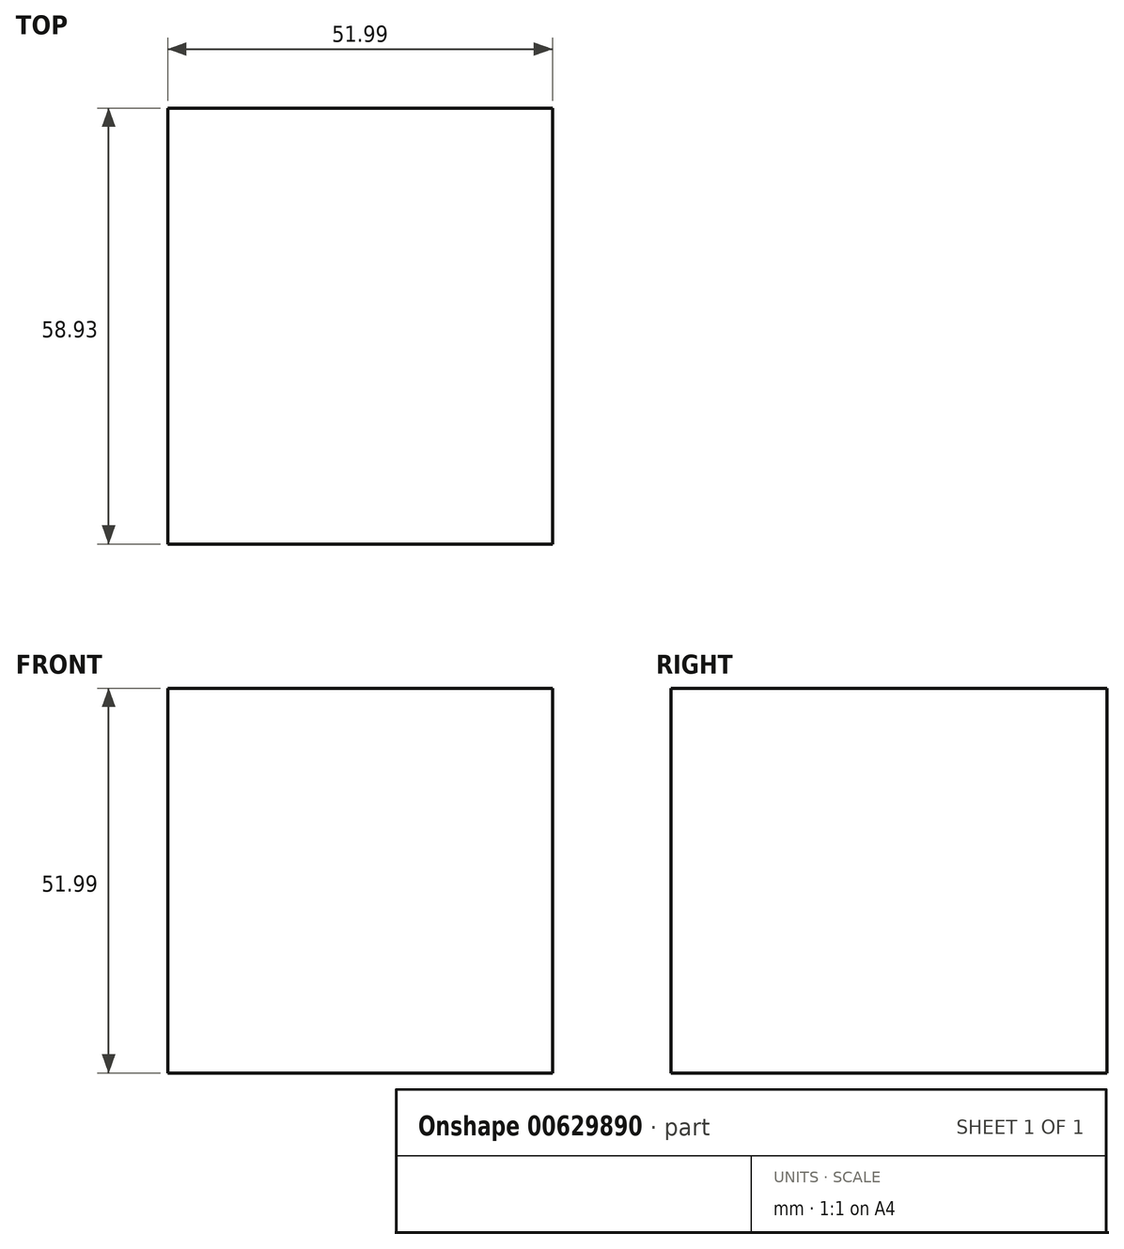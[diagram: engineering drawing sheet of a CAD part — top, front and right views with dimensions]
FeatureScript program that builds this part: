
annotation { "Feature Type Name" : "Feature", "Feature Type Description" : "" }
export const myFeature = defineFeature(function(context is Context, id is Id, definition is map)
    precondition{}
    {
        {
            var Q0;
            Q0=qCreatedBy(makeId("Front.planeOp"),FACE);
            var sketch = newSketch(context, id + "F0", { "sketchPlane" : qUnion([Q0])});
            skLineSegment(sketch, "E0.bottom", {"start": v(-3.79, 0) * mm, "end": v(-55.78, 0) * mm});
            skLineSegment(sketch, "E0.top", {"start": v(-3.79, 51.99) * mm, "end": v(-55.78, 51.99) * mm});
            skLineSegment(sketch, "E0.left", {"start": v(-3.79, 0) * mm, "end": v(-3.79, 51.99) * mm});
            skLineSegment(sketch, "E0.right", {"start": v(-55.78, 0) * mm, "end": v(-55.78, 51.99) * mm});
            skSolve(sketch);
        }
        {
            var Q0;
            Q0=makeQuery(id+"F0.imprint","IMPRINT",FACE,{"disambiguationData":[TD([[makeQuery(id+"F0.imprint","IMPRINT",EDGE,{"derivedFrom":sQuery(id+"F0.wireOp",EDGE,"E0.bottom")}),-1.0]])]});
            extrude(context, id + "F1", {"entities" : qUnion([Q0]), "depth" : 58.93 * mm, "offsetDistance" : 25.4 * mm});
        }
    });
